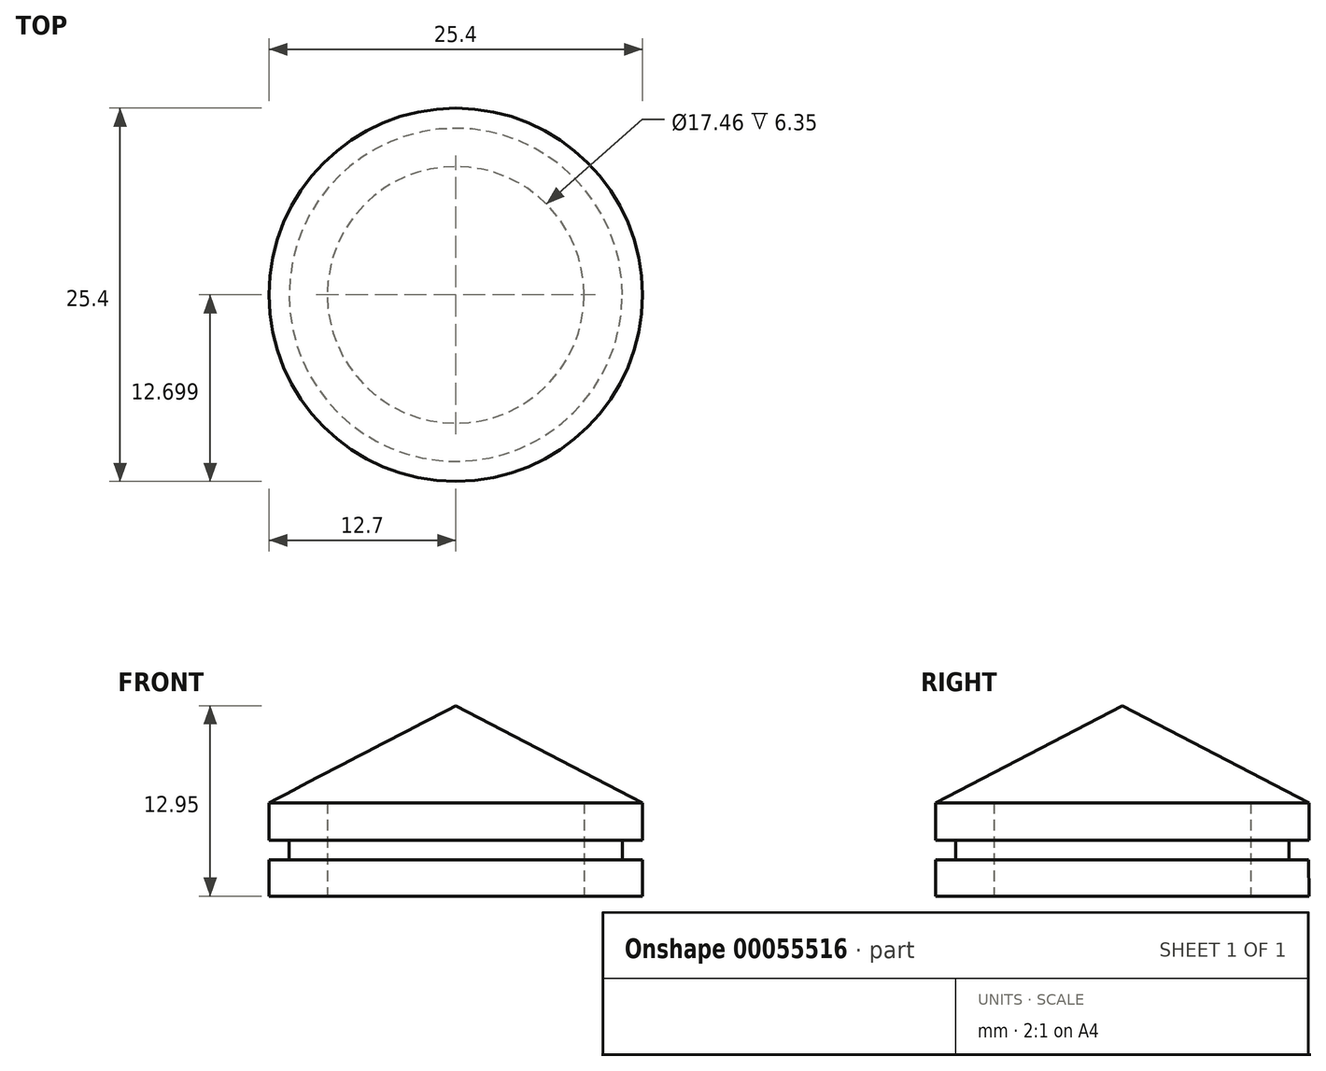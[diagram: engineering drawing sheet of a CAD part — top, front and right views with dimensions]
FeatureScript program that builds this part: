
annotation { "Feature Type Name" : "Feature", "Feature Type Description" : "" }
export const myFeature = defineFeature(function(context is Context, id is Id, definition is map)
    precondition{}
    {
        {
            var Q0;
            Q0=qCreatedBy(makeId("Right.planeOp"),FACE);
            var sketch = newSketch(context, id + "F0", { "sketchPlane" : qUnion([Q0])});
            skLineSegment(sketch, "E0", {"start": v(-27.38, 2.73) * mm, "end": v(-27.38, 0.19) * mm});
            skLineSegment(sketch, "E1", {"start": v(-27.38, 2.73) * mm, "end": v(-14.68, 9.33) * mm});
            skLineSegment(sketch, "E2", {"start": v(-27.38, -3.62) * mm, "end": v(-14.68, -3.62) * mm});
            skLineSegment(sketch, "E3", {"start": v(-27.38, 0.19) * mm, "end": v(-26.01, 0.19) * mm});
            skLineSegment(sketch, "E4", {"start": v(-26.01, 0.19) * mm, "end": v(-26.01, -1.15) * mm});
            skLineSegment(sketch, "E5", {"start": v(-26.01, -1.15) * mm, "end": v(-27.37, -1.15) * mm});
            skLineSegment(sketch, "E6", {"start": v(-27.37, -1.15) * mm, "end": v(-27.38, -3.62) * mm});
            skLineSegment(sketch, "E7", {"start": v(-14.68, 9.33) * mm, "end": v(-14.68, -3.62) * mm});
            skPoint(sketch, "E8.MirrorCS.end.orphan", {"position": v(-14.68, 9.33) * mm});
            skPoint(sketch, "E8.MirrorCS.start.orphan", {"position": v(-1.98, 2.73) * mm});
            skPoint(sketch, "E9.MirrorCS.end.orphan", {"position": v(-1.98, 0.19) * mm});
            skPoint(sketch, "E10.MirrorCS.end.orphan", {"position": v(-3.35, -1.15) * mm});
            skPoint(sketch, "E10.MirrorCS.start.orphan", {"position": v(-3.35, 0.19) * mm});
            skPoint(sketch, "E11.MirrorCS.end.orphan", {"position": v(-14.68, -3.62) * mm});
            skPoint(sketch, "E11.MirrorCS.start.orphan", {"position": v(-1.98, -3.62) * mm});
            skPoint(sketch, "E12.MirrorCS.start.orphan", {"position": v(-2, -1.15) * mm});
            skSolve(sketch);
        }
        {
            var Q0;
            Q0=makeQuery(id+"F0.imprint","IMPRINT",FACE,{"disambiguationData":[TD([[makeQuery(id+"F0.imprint","IMPRINT",EDGE,{"derivedFrom":sQuery(id+"F0.wireOp",EDGE,"E0")}),1.0]])]});
            var Q1;
            Q1=sQuery(id+"F0.wireOp",EDGE,"E7");
            revolve(context, id + "F1", {"entities" : qUnion([Q0]), "axis" : qUnion([Q1]), "revolveType" : RevolveType.FULL});
        }
        {
            var Q0;
            Q0=makeQuery(id+"F1.opRevolve","SWEPT_FACE",FACE,{"disambiguationData":[OSD([sQuery(id+"F0.wireOp",EDGE,"E2")])]});
            var sketch = newSketch(context, id + "F2", { "sketchPlane" : qUnion([Q0])});
            skCircle(sketch, "E13", {"center": v(0, 14.68) * mm, "radius": 8.73 * mm});
            skCircle(sketch, "E14", {"center": v(0, 14.68) * mm, "radius": 11.11 * mm});
            skSolve(sketch);
        }
        {
            var Q0;
            Q0=makeQuery(id+"F2.imprint","IMPRINT",FACE,{"disambiguationData":[TD([[makeQuery(id+"F2.imprint","IMPRINT",EDGE,{"derivedFrom":sQuery(id+"F2.wireOp",EDGE,"E13")}),1.0]])]});
            extrude(context, id + "F3", {"entities" : qUnion([Q0]), "operationType" : NewBodyOperationType.REMOVE, "oppositeDirection" : true, "depth" : 6.35 * mm});
        }
    });
